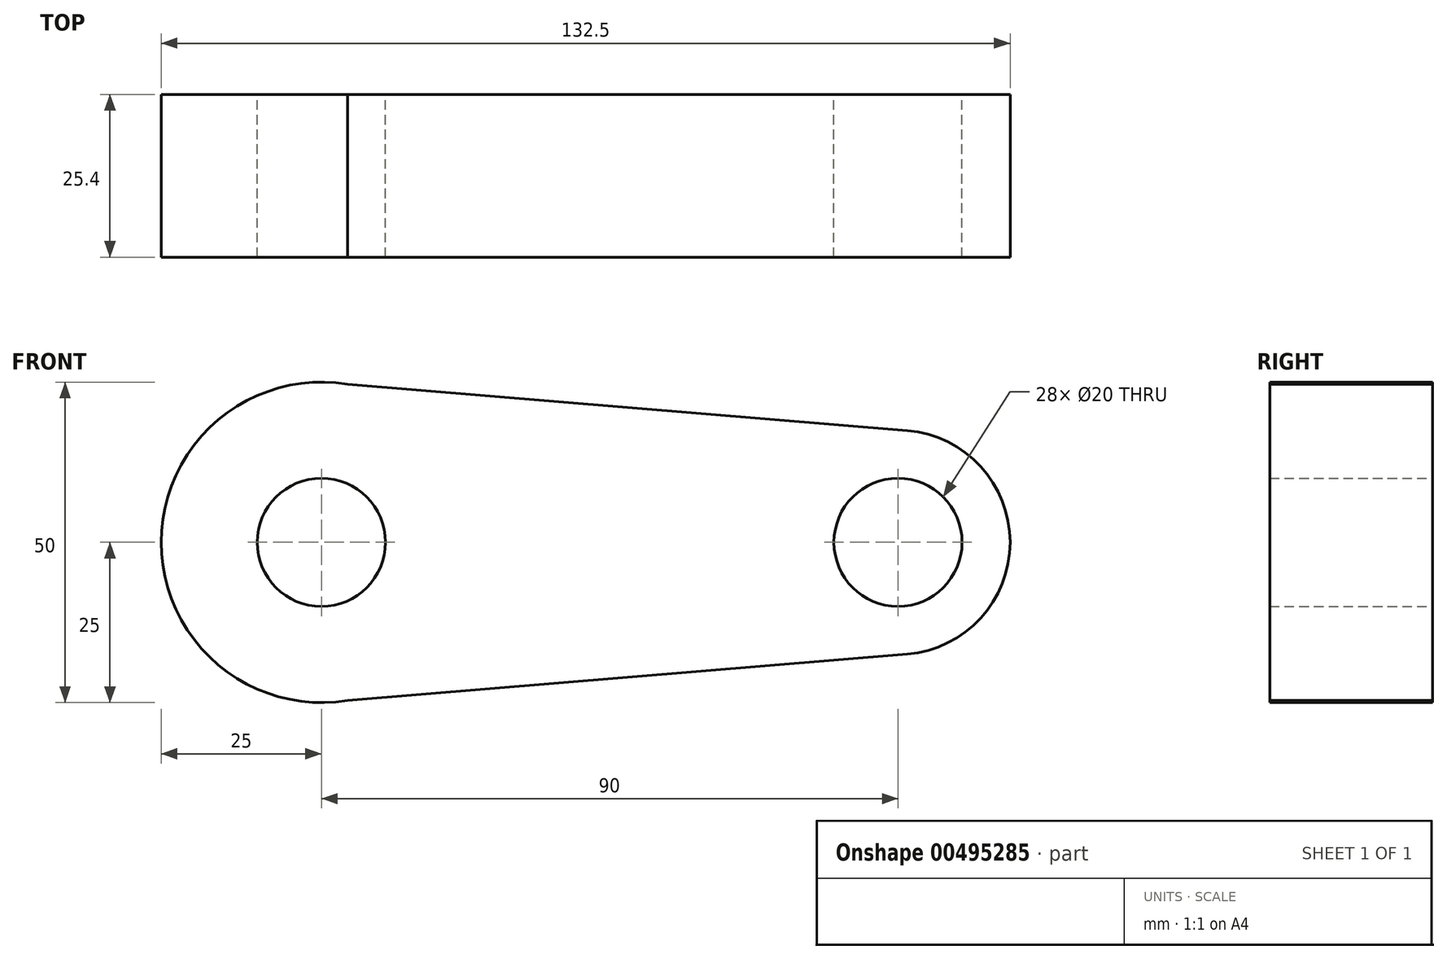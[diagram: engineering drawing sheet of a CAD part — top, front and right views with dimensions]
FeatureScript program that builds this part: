
annotation { "Feature Type Name" : "Feature", "Feature Type Description" : "" }
export const myFeature = defineFeature(function(context is Context, id is Id, definition is map)
    precondition{}
    {
        {
            var Q0;
            Q0=qCreatedBy(makeId("Front.planeOp"),FACE);
            var sketch = newSketch(context, id + "F0", { "sketchPlane" : qUnion([Q0])});
            skCircle(sketch, "E0", {"center": v(0, 0) * mm, "radius": 25 * mm});
            skCircle(sketch, "E1", {"center": v(90, 0) * mm, "radius": 17.5 * mm});
            skLineSegment(sketch, "E2", {"start": v(0, 25) * mm, "end": v(91.44, 17.44) * mm});
            skLineSegment(sketch, "E3", {"start": v(0, -25) * mm, "end": v(91.44, -17.44) * mm});
            skCircle(sketch, "E4", {"center": v(0, 0) * mm, "radius": 10 * mm});
            skCircle(sketch, "E5", {"center": v(90, 0) * mm, "radius": 10 * mm});
            skSolve(sketch);
        }
        {
            var Q0;
            Q0 = qSketchRegion(id + "F0", true);
            extrude(context, id + "F1", {"entities" : qUnion([Q0]), "depth" : 25.4 * mm});
        }
    });
